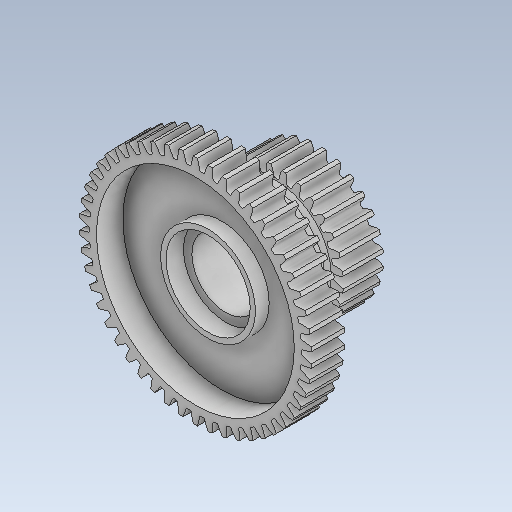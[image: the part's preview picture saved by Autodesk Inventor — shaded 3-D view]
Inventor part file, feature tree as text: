
AUTODESK INVENTOR PART (.ipt)
format: ipt  version: 2021 (Build 250183000, 183)  size: 768,512 bytes
history: native  units: in
note: dims shown in document units (in); Inventor stores cm internally (conversion verified against a paired STEP export)
features: chamfer x1
ambient origin geometry x8: Origin, YZ Plane, XZ Plane, XY Plane, X Axis, Y Axis, Z Axis, Center Point
bodies: Solid1 (feature_tree)
feature tree (1):
  chamfer  "Chamfer1"  [1 undecoded]
note: 1 required parameter value undecoded (feature->parameter linkage not recoverable at this tier; creation-order binding heuristic only, values carry confidence <= 0.55)
